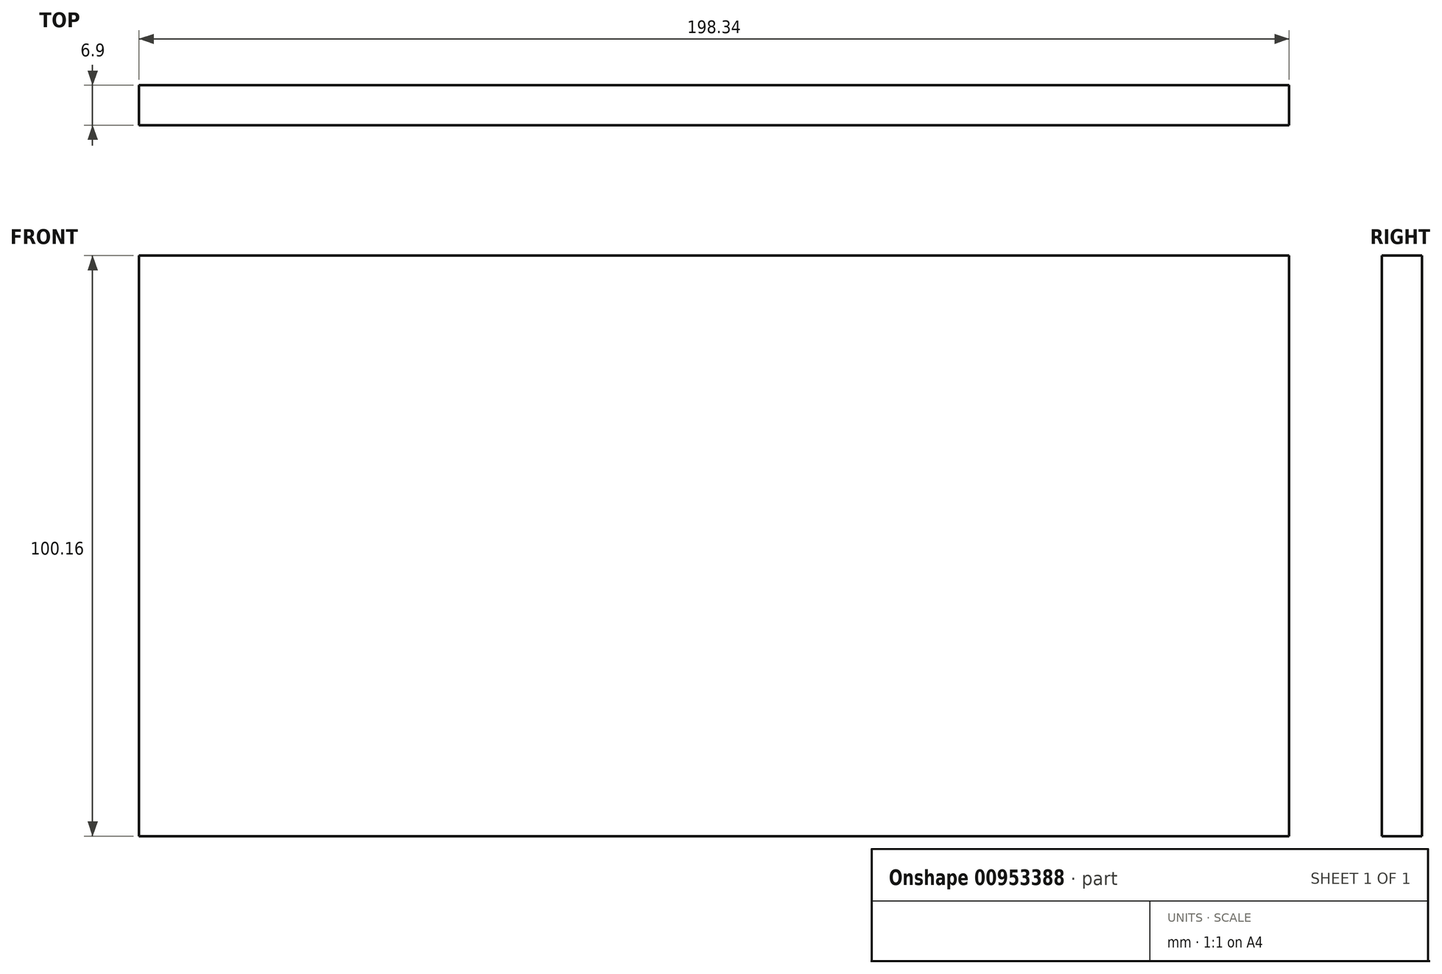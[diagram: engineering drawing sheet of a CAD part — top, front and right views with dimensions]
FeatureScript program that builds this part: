
annotation { "Feature Type Name" : "Feature", "Feature Type Description" : "" }
export const myFeature = defineFeature(function(context is Context, id is Id, definition is map)
    precondition{}
    {
        {
            var Q0;
            Q0=qCreatedBy(makeId("Front.planeOp"),FACE);
            var sketch = newSketch(context, id + "F0", { "sketchPlane" : qUnion([Q0])});
            skLineSegment(sketch, "E0.bottom", {"start": v(-99.17, 50.08) * mm, "end": v(99.17, 50.08) * mm});
            skLineSegment(sketch, "E0.top", {"start": v(-99.17, -50.08) * mm, "end": v(99.17, -50.08) * mm});
            skLineSegment(sketch, "E0.left", {"start": v(-99.17, 50.08) * mm, "end": v(-99.17, -50.08) * mm});
            skLineSegment(sketch, "E0.right", {"start": v(99.17, 50.08) * mm, "end": v(99.17, -50.08) * mm});
            skPoint(sketch, "E0.middle", {"position": v(0, 0) * mm});
            skSolve(sketch);
        }
        {
            var Q0;
            Q0=makeQuery(id+"F0.imprint","IMPRINT",FACE,{"disambiguationData":[TD([[makeQuery(id+"F0.imprint","IMPRINT",EDGE,{"derivedFrom":sQuery(id+"F0.wireOp",EDGE,"E0.bottom")}),-1.0]])]});
            extrude(context, id + "F1", {"entities" : qUnion([Q0]), "endBound" : BoundingType.SYMMETRIC, "depth" : 6.9 * mm, "offsetDistance" : 25 * mm});
        }
    });
